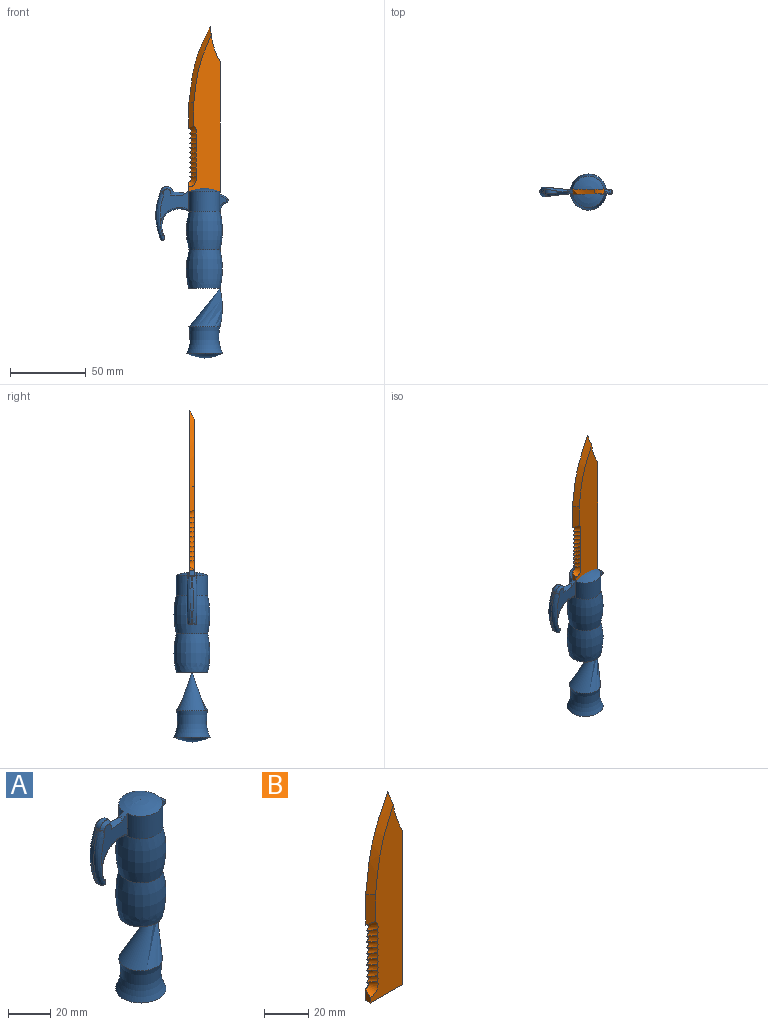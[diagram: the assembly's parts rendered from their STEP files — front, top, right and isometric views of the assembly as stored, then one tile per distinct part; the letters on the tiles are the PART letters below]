
ASSEMBLY  parts=2 mates=1
PART A: 37 faces, bbox 64.8x64.8x118.5 mm
  f0: plane 1.93x0.85mm, normal (0.11,-0.99,0), area 0.6mm2, adj f14,f22
  f1: plane 1.93x0.85mm, normal (0.11,0.99,0), area 0.6mm2, adj f14,f21
  f2: cylinder r=10.32mm len=20.64mm, axis (0,0,1), area 803mm2, adj f3,f9,f10,f11,f17,f18,f20,f25
  f3: revolved ~25.4x23.81mm, area 1834.4mm2, adj f2,f4,f8,f16
  f4: revolved ~25.4x23.81mm, area 1834.4mm2, adj f3,f5
  f5: revolved ~25.4x23.81mm, area 1834.4mm2, adj f4,f6
  f6: torus R=34.43mm, axis (0,0,1), area 1132.5mm2, adj f5,f7
  f7: sphere r=23.91mm, area 477mm2, adj f6
  f8: torus R=17.42mm, axis (0,0,1), area 8mm2, adj f3,f19,f31,f32
  f9: torus R=7.78mm, axis (0,0,1), area 6.7mm2, adj f2,f19,f29,f34
  f10: plane 7.55x4.49mm, normal (-0.11,-0.99,0), area 17.8mm2, adj f2,f29,f30,f31
  f11: plane 7.55x4.48mm, normal (-0.11,0.99,0), area 17.8mm2, adj f2,f32,f33,f34
  f12: torus R=24.94mm, axis (0,0,-1), area 28.6mm2, adj f13,f21,f22,f23,f24,f35,f36
  f13: revolved ~64.15x64.15mm, area 6357.2mm2, adj f12,f14,f21,f22
  f14: torus R=27.78mm, axis (0,0,-1), area 26mm2, adj f0,f1,f13,f15,f21,f22,f26,f27
  f15: torus R=14.75mm, axis (0,0,-1), area 54mm2, adj f14,f16,f25,f26,f27,f28
  f16: torus R=16.43mm, axis (0,0,-1), area 38.6mm2, adj f3,f15,f25,f28
  f17: plane 22.91x19.22mm, normal (0.11,-0.99,0), area 204.2mm2, adj f2,f20,f22,f24,f27,f28,f35
  f18: plane 23.32x19.63mm, normal (0.11,0.99,0), area 204.2mm2, adj f2,f20,f21,f23,f25,f26,f36
  f19: torus R=14.08mm, axis (0,0,-1), area 5.2mm2, adj f8,f9,f30,f33
  f20: sphere r=25.34mm, area 359.8mm2, adj f2,f17,f18,f35,f36
  f21: bspline ~37.8x7.6mm, area 132.5mm2, adj f1,f12,f13,f14,f18,f23,f26
  f22: bspline ~40.67x7.91mm, area 133.5mm2, adj f0,f12,f13,f14,f17,f24,f27
  f23: bspline ~8.17x6.69mm, area 24mm2, adj f12,f18,f21,f36
  f24: bspline ~8.18x7.77mm, area 24mm2, adj f12,f17,f22,f35
  f25: bspline ~19.25x7.25mm, area 29.7mm2, adj f2,f15,f16,f18,f26
  f26: bspline ~14.77x2.84mm, area 19.1mm2, adj f14,f15,f18,f21,f25
  f27: bspline ~14.77x2.84mm, area 19.1mm2, adj f14,f15,f17,f22,f28
  f28: bspline ~19.25x7.25mm, area 29.7mm2, adj f2,f15,f16,f17,f27
  f29: bspline ~6.67x3.97mm, area 6.6mm2, adj f2,f9,f10,f30
  f30: bspline ~2.81x1.47mm, area 3mm2, adj f10,f19,f29,f31
  f31: bspline ~8.3x6.75mm, area 8.1mm2, adj f2,f8,f10,f30
  f32: bspline ~8.3x6.75mm, area 8.1mm2, adj f2,f8,f11,f33
  f33: bspline ~2.81x1.47mm, area 3mm2, adj f11,f19,f32,f34
  f34: bspline ~6.5x4.31mm, area 6.6mm2, adj f2,f9,f11,f33
  f35: plane 10.01x2.88mm, normal (0.08,-0.7,0.71), area 20.6mm2, adj f12,f17,f20,f24,f36
  f36: plane 10x2.88mm, normal (0.08,0.7,0.71), area 20.6mm2, adj f12,f18,f20,f23,f35
PART B: 19 faces, bbox 22.7x5.1x113.7 mm
  f0: cylinder r=48.62mm len=23.53mm, axis (0,1,0), area 68.2mm2, adj f3,f4,f5,f18
  f1: plane 6.21x3.18mm, normal (-1,0,0), area 14.7mm2, adj f2,f4,f5,f16
  f2: plane 20.64x3.18mm, normal (0,0,-1), area 65.5mm2, adj f1,f3,f4,f5
  f3: plane 85.73x3.18mm, normal (1,0,0), area 272.2mm2, adj f0,f2,f4,f5
  f4: plane 104.75x22.45mm, normal (0,-1,0), area 1496.5mm2, adj f0,f1,f2,f3,f6,f7,f8,f9
  f5: plane 110.31x21.7mm, normal (0,1,0), area 1842.3mm2, adj f0,f1,f2,f3,f6,f7,f8,f9
  f6: cone r=1.6mm half-angle=45deg, axis (0,-1,0), area 26.8mm2, adj f4,f5,f7,f17
  f7: cone r=4.9mm half-angle=45deg, axis (0,-1,0), area 20.6mm2, adj f4,f5,f6,f8
  f8: cone r=1.6mm half-angle=45deg, axis (0,-1,0), area 20.6mm2, adj f4,f5,f7,f9
  f9: cone r=4.9mm half-angle=45deg, axis (0,-1,0), area 20.6mm2, adj f4,f5,f8,f10
  f10: cone r=1.6mm half-angle=45deg, axis (0,-1,0), area 20.6mm2, adj f4,f5,f9,f11
  f11: cone r=4.9mm half-angle=45deg, axis (0,-1,0), area 20.6mm2, adj f4,f5,f10,f12
  f12: cone r=1.6mm half-angle=45deg, axis (0,-1,0), area 20.6mm2, adj f4,f5,f11,f13
  f13: cone r=4.9mm half-angle=45deg, axis (0,-1,0), area 20.6mm2, adj f4,f5,f12,f14
  f14: cone r=1.6mm half-angle=45deg, axis (0,-1,0), area 20.6mm2, adj f4,f5,f13,f15
  f15: cone r=4.9mm half-angle=45deg, axis (0,-1,0), area 20.6mm2, adj f4,f5,f14,f16
  f16: cone r=1.6mm half-angle=45deg, axis (0,-1,0), area 33.7mm2, adj f1,f4,f5,f15
  f17: plane 17.89x4.04mm, normal (-0.71,-0.71,0), area 71.3mm2, adj f4,f5,f6,f18
  f18: bspline ~56.07x18.66mm, area 222.4mm2, adj f0,f4,f5,f17
PLACE A t=(-18.81,14.17,-11.19)mm
PLACE B t=(-17.22,15.76,95.64)mm
MATE fastened B.f2 <-> A.f6  axis (0,0,-1) through (-6.9,14.17,95.64)mm
